# Revit family: KEUCO_14958010037
name_source: partatom
category: Sonderausstattung
revit_build: Autodesk Revit 2016 (Build: 20150220_1215(x64)
units: mm (PartAtom-declared; Revit-internal decimal feet)

## family parameters
Arbeitsebenenbasiert = Nein
Beim Laden mit Abzugskörper schneiden = Nein
Bemaßung runder Anschluss = Durchmesser verwenden
Gemeinsam genutzt = Nein
Immer vertikal = Ja
Raumberechnungspunkt = Nein
Teiletyp = Normal

## types (9) — shared parameters
Beschreibung = 2-teilig: Metallkorb und herausnehmbarer,
seifenbeständiger, bruchfester und
UV-unempfindlicher Kunststoff-Einsatz
Gewicht = 382
Hersteller = KEUCO
Kategorie = ACC
Preisgruppe = 1
Serie = Plan
URL = https://www.keuco.com
Verwendung = DU / WA

## per-type parameters (varying)
| type | Ausschreibungstext | Material Regal |
| 14958010037 | KEUCO PLAN Duschkorb, 14958010037
hochglanzverchromter Duschkorb in ästhetischem, funktionalem Design, 
verchromt/schwarzgrau (RAL 7021),
hochwertiger Metallrahmen mit herausnehmbaren, 
seifenbeständigem, bruchfestem und 
UV-unempfindlichen Kunststoff-Einsatz(Polysterol schlagzäh),
Tiefe 102 mm, Breite 288, Höhe 29 mm, 
Befestigungsabstand 160 mm,
der Duschkorb wird verdeckt angebracht,
Lieferung inkl. korrosionsfreiem Befestigungsmaterial | Schwarzgrau  (RAL 7021) |
| 14958010038 | KEUCO PLAN Duschkorb, 14958010038
hochglanzverchromter Duschkorb in ästhetischem, funktionalem Design, 
verchromt/lichtgrau (RAL 7035),
hochwertiger Metallrahmen mit herausnehmbaren, 
seifenbeständigem, bruchfestem und 
UV-unempfindlichen Kunststoff-Einsatz (Polysterol schlagzäh),
Tiefe 102 mm, Breite 288, Höhe 29 mm, 
Befestigungsabstand 160 mm,
der Duschkorb wird verdeckt angebracht,
Lieferung inkl. korrosionsfreiem Befestigungsmaterial | Lichtgrau (RAL 7035) |
| 14958010051 | KEUCO PLAN Duschkorb, 14958010051
hochglanzverchromter Duschkorb in ästhetischem, funktionalem Design, 
verchromt/weiß (RAL 9010),
hochwertiger Metallrahmen mit herausnehmbaren, 
seifenbeständigem, bruchfestem und 
UV-unempfindlichen Kunststoff-Einsatz (Polysterol schlagzäh),
Tiefe 102 mm, Breite 288, Höhe 29 mm, 
Befestigungsabstand 160 mm,
der Duschkorb wird verdeckt angebracht,
Lieferung inkl. korrosionsfreiem Befestigungsmaterial | Weiß (RAL 9010) |
| 14958070037 | KEUCO PLAN Duschkorb, 14958070037
Duschkorb in Edelstahl-Optik in ästhetischem, funktionalem Design, 
Edelstahl-finish/schwarzgrau (RAL 7021),
hochwertiger Metallrahmen mit herausnehmbaren, 
seifenbeständigem, bruchfestem und 
UV-unempfindlichen Kunststoff-Einsatz(Polysterol schlagzäh),
Tiefe 102 mm, Breite 288, Höhe 29 mm, 
Befestigungsabstand 160 mm,
der Duschkorb wird verdeckt angebracht,
Lieferung inkl. korrosionsfreiem Befestigungsmaterial | Schwarzgrau  (RAL 7021) |
| 14958070038 | KEUCO PLAN Duschkorb, 14958070038
Duschkorb in Edelstahl-Optik in ästhetischem, funktionalem Design, 
Edelstahl-finish/lichtgrau (RAL 7035),
hochwertiger Metallrahmen mit herausnehmbaren, 
seifenbeständigem, bruchfestem und 
UV-unempfindlichen Kunststoff-Einsatz (Polysterol schlagzäh),
Tiefe 102 mm, Breite 288, Höhe 29 mm, 
Befestigungsabstand 160 mm,
der Duschkorb wird verdeckt angebracht,
Lieferung inkl. korrosionsfreiem Befestigungsmaterial | Lichtgrau (RAL 7035) |
| 14958070051 | KEUCO PLAN Duschkorb, 14958070051
Duschkorb in Edelstahl-Optik in ästhetischem, funktionalem Design, 
Edelstahl-finish/weiß (RAL 9010),
hochwertiger Metallrahmen mit herausnehmbaren, 
seifenbeständigem, bruchfestem und 
UV-unempfindlichen Kunststoff-Einsatz (Polysterol schlagzäh),
Tiefe 102 mm, Breite 288, Höhe 29 mm, 
Befestigungsabstand 160 mm,
der Duschkorb wird verdeckt angebracht,
Lieferung inkl. korrosionsfreiem Befestigungsmaterial | Weiß (RAL 9010) |
| 14958170037 | KEUCO PLAN Duschkorb, 14958170037
Duschkorb in Aluminium-Optik in ästhetischem, funktionalem Design, 
Aluminium-finish/schwarzgrau (RAL 7021),
hochwertiger Metallrahmen mit herausnehmbaren, 
seifenbeständigem, bruchfestem und 
UV-unempfindlichen Kunststoff-Einsatz (Polysterol schlagzäh),
Tiefe 102 mm, Breite 288, Höhe 29 mm, 
Befestigungsabstand 160 mm,
der Duschkorb wird verdeckt angebracht,
Lieferung inkl. korrosionsfreiem Befestigungsmaterial | Weiß (RAL 9010) |
| 14958170038 | KEUCO PLAN Duschkorb, 14958170038
Duschkorb in Aluminium-Optik in ästhetischem, funktionalem Design, 
Aluminium-finish/lichtgrau (RAL 7035),
hochwertiger Metallrahmen mit herausnehmbaren, 
seifenbeständigem, bruchfestem und 
UV-unempfindlichen Kunststoff-Einsatz (Polysterol schlagzäh),
Tiefe 102 mm, Breite 288, Höhe 29 mm, 
Befestigungsabstand 160 mm,
der Duschkorb wird verdeckt angebracht,
Lieferung inkl. korrosionsfreiem Befestigungsmaterial | Lichtgrau (RAL 7035) |
| 14958170051 | KEUCO PLAN Duschkorb, 14958170051
Duschkorb in Aluminium-Optik in ästhetischem, funktionalem Design, 
Aluminium-finish/weiß (RAL 9010),
hochwertiger Metallrahmen mit herausnehmbaren, 
seifenbeständigem, bruchfestem und 
UV-unempfindlichen Kunststoff-Einsatz (Polysterol schlagzäh),
Tiefe 102 mm, Breite 288, Höhe 29 mm, 
Befestigungsabstand 160 mm,
der Duschkorb wird verdeckt angebracht,
Lieferung inkl. korrosionsfreiem Befestigungsmaterial | Weiß (RAL 9010) |

note: column(s) folded — value = type name in every type: Artikelnummer

## geometry (parser evidence)
native form markers: Blend x4, Sweep x2
no freeform markers — native parametric forms only
